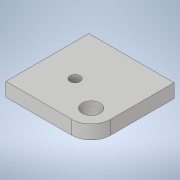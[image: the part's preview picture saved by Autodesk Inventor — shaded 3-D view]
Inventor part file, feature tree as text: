
AUTODESK INVENTOR PART (.ipt)
format: ipt  version: 2021 (Build 250183000, 183)  size: 118,272 bytes
history: native  units: mm
features: sketch x5, hole x2, other x1, extrude x1, fillet x1
ambient origin geometry x8: Origin, YZ Plane, XZ Plane, XY Plane, X Axis, Y Axis, Z Axis, Center Point
bodies: Body1 (feature_tree)
feature tree (10):
  other  "Твердое тело1"
  extrude  "Выдавливание1"  Depth=185.0mm
  fillet  "Сопряжение1"  Radius=180.0mm
  hole  "Отверстие5"  [1 undecoded]
  hole  "Отверстие7"  [1 undecoded]
  sketch  "Эскиз1"
  sketch  "Эскиз3"
  sketch  "Эскиз4"
  sketch  "Эскиз7"
  sketch  "Эскиз9"
note: 2 required parameter values undecoded (feature->parameter linkage not recoverable at this tier; creation-order binding heuristic only, values carry confidence <= 0.55)
